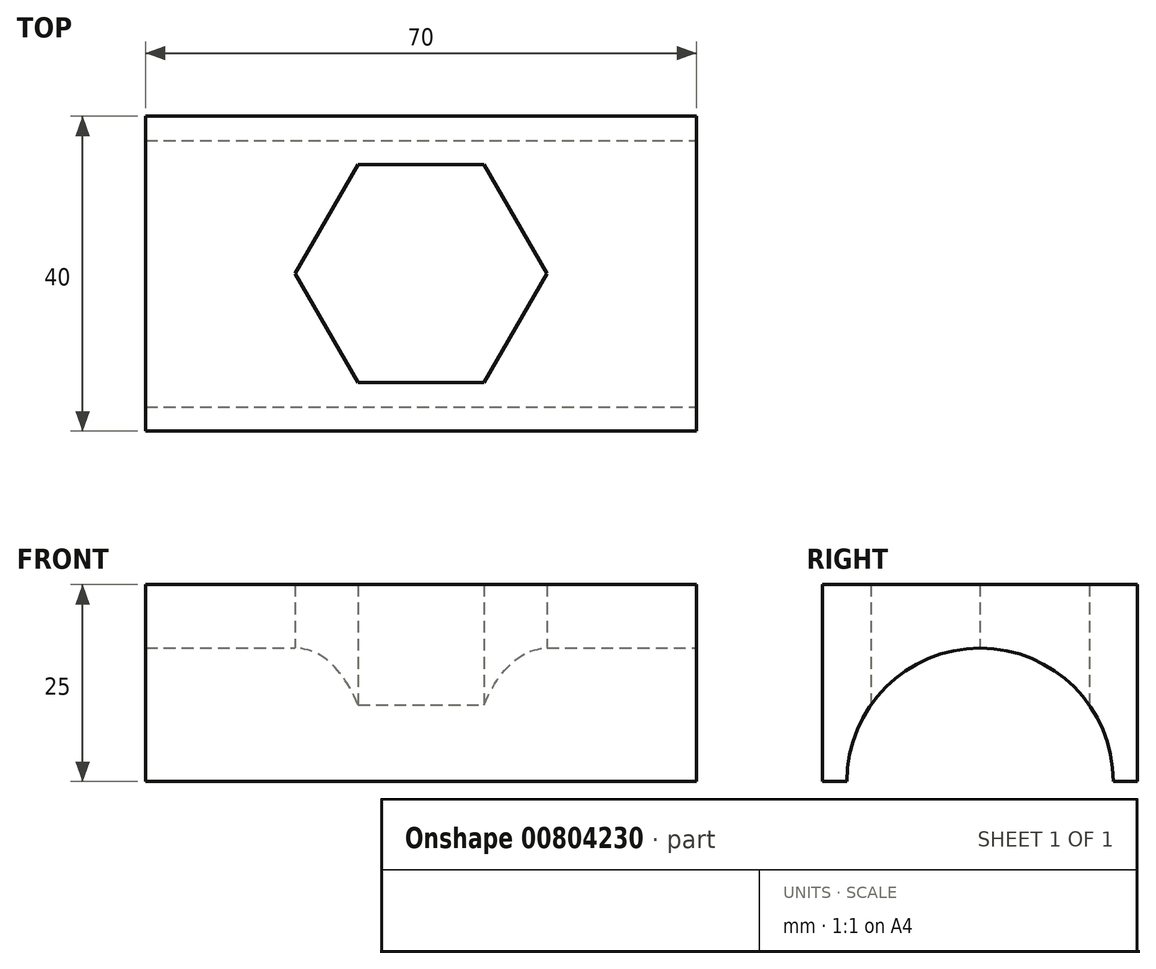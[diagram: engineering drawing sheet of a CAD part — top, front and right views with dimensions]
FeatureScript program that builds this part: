
annotation { "Feature Type Name" : "Feature", "Feature Type Description" : "" }
export const myFeature = defineFeature(function(context is Context, id is Id, definition is map)
    precondition{}
    {
        {
            var Q0;
            Q0=qCreatedBy(makeId("Top.planeOp"),FACE);
            var sketch = newSketch(context, id + "F0", { "sketchPlane" : qUnion([Q0])});
            skLineSegment(sketch, "E0.bottom", {"start": v(35, 20) * mm, "end": v(-35, 20) * mm});
            skLineSegment(sketch, "E0.top", {"start": v(35, -20) * mm, "end": v(-35, -20) * mm});
            skLineSegment(sketch, "E0.left", {"start": v(35, 20) * mm, "end": v(35, -20) * mm});
            skLineSegment(sketch, "E0.right", {"start": v(-35, 20) * mm, "end": v(-35, -20) * mm});
            skPoint(sketch, "E0.middle", {"position": v(0, 0) * mm});
            skCircle(sketch, "E1.cCircle", {"center": v(0, 0) * mm, "radius": 16 * mm, "construction": true});
            skLineSegment(sketch, "E1.0", {"start": v(-16, 0) * mm, "end": v(-8, 13.86) * mm});
            skLineSegment(sketch, "E1.1", {"start": v(-8, 13.86) * mm, "end": v(8, 13.86) * mm});
            skLineSegment(sketch, "E1.2", {"start": v(8, 13.86) * mm, "end": v(16, 0) * mm});
            skLineSegment(sketch, "E1.3", {"start": v(16, 0) * mm, "end": v(8, -13.86) * mm});
            skLineSegment(sketch, "E1.4", {"start": v(8, -13.86) * mm, "end": v(-8, -13.86) * mm});
            skLineSegment(sketch, "E1.5", {"start": v(-8, -13.86) * mm, "end": v(-16, 0) * mm});
            skSolve(sketch);
        }
        {
            var Q0;
            Q0 = qSketchRegion(id + "F0", true);
            extrude(context, id + "F1", {"entities" : qUnion([Q0]), "depth" : 25 * mm, "offsetDistance" : 25 * mm});
        }
        {
            var Q0;
            Q0=makeQuery(id+"F1.opExtrude","SWEPT_FACE",FACE,{"disambiguationData":[OSD([sQuery(id+"F0.wireOp",EDGE,"E0.left")])]});
            var sketch = newSketch(context, id + "F2", { "sketchPlane" : qUnion([Q0])});
            skCircle(sketch, "E2", {"center": v(0, 0) * mm, "radius": 16.92 * mm});
            skSolve(sketch);
        }
        {
            var Q0;
            {var subQ0=sQuery(id+"F2.wireOp",EDGE,"E2");var subQ1=makeQuery(id+"F1.opExtrude","CAP_EDGE",EDGE,{"disambiguationData":[OSD([sQuery(id+"F0.wireOp",EDGE,"E0.left")])],"isStart":true});var subQ2=makeQuery(id+"F2.imprint","INTERSECT",VERTEX,{"disambiguationData":[OD(0.0)],"derivedFrom":[subQ1,subQ0]});Q0=makeQuery(id+"F2.imprint","IMPRINT",FACE,{"disambiguationData":[TD([[makeQuery(id+"F2.imprint","IMPRINT",EDGE,{"disambiguationData":[TD([[subQ2,1.0]])],"derivedFrom":subQ0}),1.0]])]});}
            var Q1;
            {var subQ0=sQuery(id+"F2.wireOp",EDGE,"E2");var subQ1=makeQuery(id+"F1.opExtrude","CAP_EDGE",EDGE,{"disambiguationData":[OSD([sQuery(id+"F0.wireOp",EDGE,"E0.left")])],"isStart":true});var subQ2=makeQuery(id+"F2.imprint","INTERSECT",VERTEX,{"disambiguationData":[OD(0.0)],"derivedFrom":[subQ1,subQ0]});Q1=makeQuery(id+"F2.imprint","IMPRINT",FACE,{"disambiguationData":[TD([[makeQuery(id+"F2.imprint","IMPRINT",EDGE,{"disambiguationData":[TD([[subQ2,-1.0]])],"derivedFrom":subQ0}),1.0]])]});}
            extrude(context, id + "F3", {"entities" : qUnion([Q0, Q1]), "operationType" : NewBodyOperationType.REMOVE, "endBound" : BoundingType.THROUGH_ALL, "oppositeDirection" : true, "depth" : 25 * mm, "offsetDistance" : 25 * mm});
        }
    });
